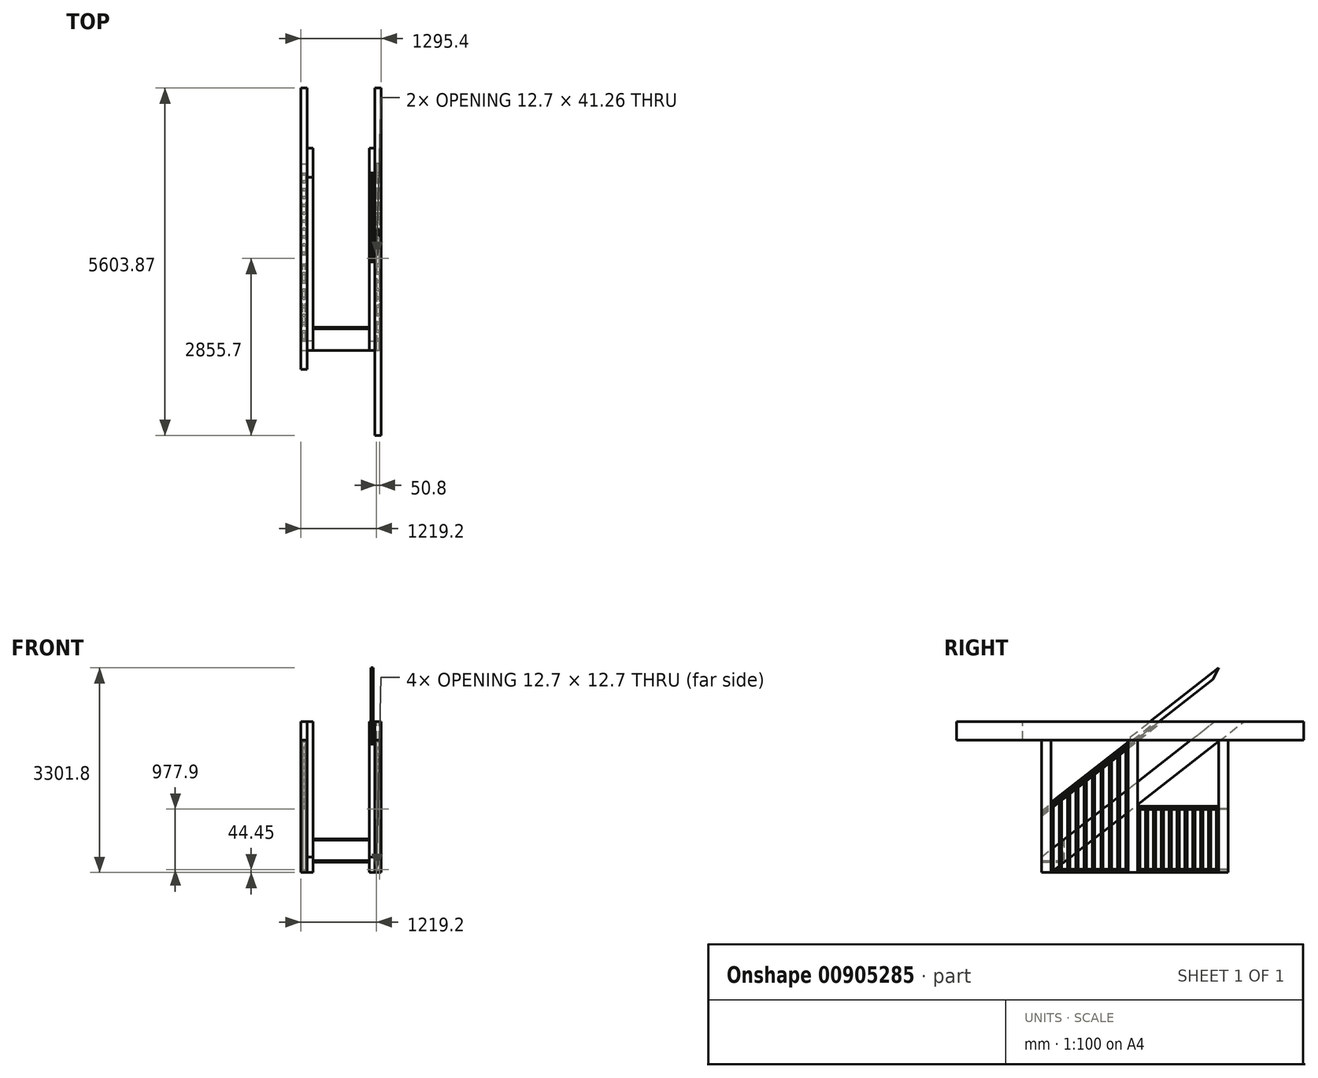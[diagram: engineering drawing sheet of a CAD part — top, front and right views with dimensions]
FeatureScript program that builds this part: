
annotation { "Feature Type Name" : "Feature", "Feature Type Description" : "" }
export const myFeature = defineFeature(function(context is Context, id is Id, definition is map)
    precondition{}
    {
        {
            var Q0;
            Q0=qCreatedBy(makeId("Front.planeOp"),FACE);
            var sketch = newSketch(context, id + "F0", { "sketchPlane" : qUnion([Q0])});
            skLineSegment(sketch, "E0", {"start": v(-546.1, 0) * mm, "end": v(546.1, 0) * mm});
            skSolve(sketch);
        }
        {
            var Q0;
            Q0=sQuery(id+"F0.wireOp",VERTEX,"E0.end");
            var Q1;
            Q1=qCreatedBy(makeId("Right.planeOp"),FACE);
            cPlane(context, id + "F1", {"entities" : qUnion([Q0, Q1]), "cplaneType" : CPlaneType.PLANE_POINT, "offset" : 25.4 * mm, "width" : 152.4 * mm, "height" : 152.4 * mm});
        }
        {
            var Q0;
            Q0=qCreatedBy(id+"F1.planeOp",FACE);
            var sketch = newSketch(context, id + "F2", { "sketchPlane" : qUnion([Q0])});
            skLineSegment(sketch, "E1.bottom", {"start": v(0, 0) * mm, "end": v(152.4, 0) * mm});
            skLineSegment(sketch, "E1.top", {"start": v(0, 2133.6) * mm, "end": v(152.4, 2133.6) * mm});
            skLineSegment(sketch, "E1.left", {"start": v(0, 0) * mm, "end": v(0, 2133.6) * mm});
            skLineSegment(sketch, "E1.right", {"start": v(152.4, 0) * mm, "end": v(152.4, 2133.6) * mm});
            skLineSegment(sketch, "E2.bottom", {"start": v(1397, 0) * mm, "end": v(1552.58, 0) * mm});
            skLineSegment(sketch, "E2.top", {"start": v(1397, 2133.6) * mm, "end": v(1552.57, 2133.6) * mm});
            skLineSegment(sketch, "E2.left", {"start": v(1397, 0) * mm, "end": v(1397, 2133.6) * mm});
            skLineSegment(sketch, "E2.right", {"start": v(1552.58, 0) * mm, "end": v(1552.57, 2133.6) * mm});
            skLineSegment(sketch, "E3.bottom", {"start": v(2860.68, 0) * mm, "end": v(3013.08, 0) * mm});
            skLineSegment(sketch, "E3.top", {"start": v(2860.68, 2133.6) * mm, "end": v(3013.07, 2133.6) * mm});
            skLineSegment(sketch, "E3.left", {"start": v(2860.68, 0) * mm, "end": v(2860.68, 2133.6) * mm});
            skLineSegment(sketch, "E3.right", {"start": v(3013.08, 0) * mm, "end": v(3013.07, 2133.6) * mm});
            skLineSegment(sketch, "E4.bottom", {"start": v(-1371.6, 2432.05) * mm, "end": v(4232.28, 2432.05) * mm});
            skLineSegment(sketch, "E4.top", {"start": v(-1371.6, 2133.6) * mm, "end": v(4232.28, 2133.6) * mm, "construction": true});
            skLineSegment(sketch, "E4.left", {"start": v(-1371.6, 2432.05) * mm, "end": v(-1371.6, 2133.6) * mm});
            skLineSegment(sketch, "E4.right", {"start": v(4232.28, 2432.05) * mm, "end": v(4232.28, 2133.6) * mm});
            skSolve(sketch);
        }
        {
            var Q0;
            Q0=qSketchRegion(id+"F2",true);
            extrude(context, id + "F3", {"entities" : qUnion([Q0]), "depth" : 101.6 * mm, "offsetDistance" : 25.4 * mm});
        }
        {
            var Q0;
            Q0=sQuery(id+"F0.wireOp",VERTEX,"E0.start");
            var Q1;
            Q1=qCreatedBy(makeId("Right.planeOp"),FACE);
            cPlane(context, id + "F4", {"entities" : qUnion([Q0, Q1]), "cplaneType" : CPlaneType.PLANE_POINT, "offset" : 25.4 * mm, "width" : 152.4 * mm, "height" : 152.4 * mm});
        }
        {
            var Q0;
            Q0=qCreatedBy(id+"F4.planeOp",FACE);
            var sketch = newSketch(context, id + "F5", { "sketchPlane" : qUnion([Q0])});
            skLineSegment(sketch, "E5.bottom", {"start": v(1390.65, 0) * mm, "end": v(1543.05, 0) * mm});
            skLineSegment(sketch, "E5.top", {"start": v(1390.65, 2133.6) * mm, "end": v(1543.05, 2133.6) * mm});
            skLineSegment(sketch, "E5.left", {"start": v(1390.65, 0) * mm, "end": v(1390.65, 2133.6) * mm});
            skLineSegment(sketch, "E5.right", {"start": v(1543.05, 0) * mm, "end": v(1543.05, 2133.6) * mm});
            skLineSegment(sketch, "E6.bottom", {"start": v(2863.85, 0) * mm, "end": v(3009.9, 0) * mm});
            skLineSegment(sketch, "E6.top", {"start": v(2863.85, 2133.6) * mm, "end": v(3009.9, 2133.6) * mm});
            skLineSegment(sketch, "E6.left", {"start": v(2863.85, 0) * mm, "end": v(2863.85, 2133.6) * mm});
            skLineSegment(sketch, "E6.right", {"start": v(3009.9, 0) * mm, "end": v(3009.9, 2133.6) * mm});
            skLineSegment(sketch, "E7.0.0", {"start": v(152.4, 2133.6) * mm, "end": v(0, 2133.6) * mm});
            skLineSegment(sketch, "E7.0.1", {"start": v(0, 2133.6) * mm, "end": v(0, 0) * mm});
            skLineSegment(sketch, "E7.0.2", {"start": v(0, 0) * mm, "end": v(152.4, 0) * mm});
            skLineSegment(sketch, "E7.0.3", {"start": v(152.4, 0) * mm, "end": v(152.4, 2133.6) * mm});
            skSolve(sketch);
        }
        {
            var Q0;
            Q0=qSketchRegion(id+"F5",true);
            extrude(context, id + "F6", {"entities" : qUnion([Q0]), "oppositeDirection" : true, "depth" : 101.6 * mm, "offsetDistance" : 25.4 * mm});
        }
        {
            var Q0;
            Q0=qCreatedBy(id+"F1.planeOp",FACE);
            var sketch = newSketch(context, id + "F7", { "sketchPlane" : qUnion([Q0])});
            skLineSegment(sketch, "E8.0", {"start": v(-1371.6, 2133.6) * mm, "end": v(4232.28, 2133.6) * mm});
            skLineSegment(sketch, "E9.0", {"start": v(-1371.6, 2432.05) * mm, "end": v(-1371.6, 2133.6) * mm});
            skLineSegment(sketch, "E10.0", {"start": v(-1371.6, 2432.05) * mm, "end": v(4232.28, 2432.05) * mm});
            skLineSegment(sketch, "E11.0", {"start": v(4232.28, 2432.05) * mm, "end": v(4232.28, 2133.6) * mm});
            skSolve(sketch);
        }
        {
            var Q0;
            Q0=makeQuery(id+"F7.imprint","IMPRINT",FACE,{"disambiguationData":[TD([[makeQuery(id+"F7.imprint","IMPRINT",EDGE,{"derivedFrom":sQuery(id+"F7.wireOp",EDGE,"E8.0")}),1.0]])]});
            var Q1;
            Q1=makeQuery(id+"F3.opExtrude","CAP_FACE",FACE,{"disambiguationData":[OSD([sQuery(id+"F2.wireOp",EDGE,"E1.bottom"),sQuery(id+"F2.wireOp",EDGE,"E1.top"),sQuery(id+"F2.wireOp",EDGE,"E1.left"),sQuery(id+"F2.wireOp",EDGE,"E1.right")])],"isStart":false});
            extrude(context, id + "F8", {"entities" : qUnion([Q0]), "endBound" : BoundingType.UP_TO_SURFACE, "depth" : 25.4 * mm, "endBoundEntityFace" : qUnion([Q1]), "offsetDistance" : 25.4 * mm});
        }
        {
            var Q0;
            Q0=qCreatedBy(id+"F4.planeOp",FACE);
            var sketch = newSketch(context, id + "F9", { "sketchPlane" : qUnion([Q0])});
            skLineSegment(sketch, "E12.0.0", {"start": v(4232.28, 2432.05) * mm, "end": v(4232.28, 2133.6) * mm});
            skLineSegment(sketch, "E12.0.1", {"start": v(4232.28, 2133.6) * mm, "end": v(-304.8, 2133.6) * mm});
            skLineSegment(sketch, "E12.0.3", {"start": v(-304.8, 2432.05) * mm, "end": v(4232.28, 2432.05) * mm});
            skLineSegment(sketch, "E13", {"start": v(-304.8, 2432.05) * mm, "end": v(-304.8, 2133.6) * mm});
            skPoint(sketch, "E12.0.2.end.orphan", {"position": v(-1371.6, 2432.05) * mm});
            skPoint(sketch, "E14.orphan", {"position": v(-1371.6, 2133.6) * mm});
            skSolve(sketch);
        }
        {
            var Q0;
            Q0=qSketchRegion(id+"F9",true);
            var Q1;
            Q1=makeQuery(id+"F6.opExtrude","CAP_FACE",FACE,{"disambiguationData":[OSD([sQuery(id+"F5.wireOp",EDGE,"E7.0.0"),sQuery(id+"F5.wireOp",EDGE,"E7.0.1"),sQuery(id+"F5.wireOp",EDGE,"E7.0.2"),sQuery(id+"F5.wireOp",EDGE,"E7.0.3")])],"isStart":false});
            extrude(context, id + "F10", {"entities" : qUnion([Q0]), "endBound" : BoundingType.UP_TO_SURFACE, "oppositeDirection" : true, "depth" : 25.4 * mm, "endBoundEntityFace" : qUnion([Q1]), "offsetDistance" : 25.4 * mm});
        }
        {
            var Q0;
            Q0=qCreatedBy(id+"F1.planeOp",FACE);
            var sketch = newSketch(context, id + "F11", { "sketchPlane" : qUnion([Q0])});
            skLineSegment(sketch, "E15.0", {"start": v(0, 0) * mm, "end": v(0, 251.61) * mm});
            skLineSegment(sketch, "E16", {"start": v(0, 251.61) * mm, "end": v(2790.83, 2432.05) * mm});
            skLineSegment(sketch, "E17", {"start": v(152.4, 0) * mm, "end": v(3265.28, 2432.05) * mm});
            skPoint(sketch, "E18.orphan", {"position": v(0, 2133.6) * mm});
            skPoint(sketch, "E19.orphan", {"position": v(152.4, 2133.6) * mm});
            skLineSegment(sketch, "E20.0", {"start": v(0, 0) * mm, "end": v(152.4, 0) * mm});
            skLineSegment(sketch, "E21.0", {"start": v(2790.83, 2432.05) * mm, "end": v(3265.28, 2432.05) * mm});
            skPoint(sketch, "E22.orphan", {"position": v(4232.28, 2432.05) * mm});
            skPoint(sketch, "E23.orphan", {"position": v(-1371.6, 2432.05) * mm});
            skPoint(sketch, "E24.0.end.orphan", {"position": v(3013.07, 2133.6) * mm});
            skPoint(sketch, "E24.0.start.orphan", {"position": v(3013.08, 0) * mm});
            skSolve(sketch);
        }
        {
            var Q0;
            Q0=qSketchRegion(id+"F11",true);
            extrude(context, id + "F12", {"entities" : qUnion([Q0]), "oppositeDirection" : true, "depth" : 92.07 * mm, "offsetDistance" : 25.4 * mm});
        }
        {
            var Q0;
            Q0=makeQuery(id+"F12.opExtrude","SWEPT_BODY",BODY,{"disambiguationData":[OSD([sQuery(id+"F11.wireOp",EDGE,"E15.0"),sQuery(id+"F11.wireOp",EDGE,"E16"),sQuery(id+"F11.wireOp",EDGE,"E17"),sQuery(id+"F11.wireOp",EDGE,"E20.0"),sQuery(id+"F11.wireOp",EDGE,"E21.0")])]});
            var Q1;
            Q1=qCreatedBy(makeId("Right.planeOp"),FACE);
            mirror(context, id + "F13", {"entities" : qUnion([Q0]), "mirrorPlane" : qUnion([Q1])});
        }
        {
            var Q0;
            Q0=makeQuery(id+"F3.opExtrude","CAP_FACE",FACE,{"disambiguationData":[OSD([sQuery(id+"F2.wireOp",EDGE,"E1.bottom"),sQuery(id+"F2.wireOp",EDGE,"E1.top"),sQuery(id+"F2.wireOp",EDGE,"E1.left"),sQuery(id+"F2.wireOp",EDGE,"E1.right")])],"isStart":false});
            var Q1;
            Q1=makeQuery(id+"F2.imprint","IMPRINT",FACE,{"disambiguationData":[TD([[makeQuery(id+"F2.imprint","IMPRINT",EDGE,{"derivedFrom":sQuery(id+"F2.wireOp",EDGE,"E1.bottom")}),1.0]])]});
            cPlane(context, id + "F14", {"entities" : qUnion([Q0, Q1]), "cplaneType" : CPlaneType.MID_PLANE, "offset" : 25.4 * mm, "width" : 152.4 * mm, "height" : 152.4 * mm});
        }
        {
            var Q0;
            Q0=qCreatedBy(id+"F14.planeOp",FACE);
            var sketch = newSketch(context, id + "F15", { "sketchPlane" : qUnion([Q0])});
            skLineSegment(sketch, "E25.0", {"start": v(152.4, 1028.7) * mm, "end": v(152.4, 1066.8) * mm, "construction": true});
            skLineSegment(sketch, "E26.0", {"start": v(1397, 1028.7) * mm, "end": v(1397, 1066.8) * mm, "construction": true});
            skLineSegment(sketch, "E27.bottom", {"start": v(152.4, 1066.8) * mm, "end": v(1397, 1066.8) * mm, "construction": true});
            skLineSegment(sketch, "E27.top", {"start": v(152.4, 1028.7) * mm, "end": v(1397, 1028.7) * mm, "construction": true});
            skPoint(sketch, "E28.orphan", {"position": v(152.4, 2133.6) * mm});
            skPoint(sketch, "E29.orphan", {"position": v(1397, 2133.6) * mm});
            skPoint(sketch, "E30.orphan", {"position": v(1397, 0) * mm});
            skPoint(sketch, "E31.orphan", {"position": v(152.4, 0) * mm});
            skLineSegment(sketch, "E32.bottom", {"start": v(1552.58, 1066.8) * mm, "end": v(2860.68, 1066.8) * mm});
            skLineSegment(sketch, "E32.top", {"start": v(1552.58, 1028.7) * mm, "end": v(2860.68, 1028.7) * mm});
            skLineSegment(sketch, "E32.left", {"start": v(1552.58, 1066.8) * mm, "end": v(1552.58, 1028.7) * mm});
            skLineSegment(sketch, "E32.right", {"start": v(2860.68, 1066.8) * mm, "end": v(2860.68, 1028.7) * mm});
            skLineSegment(sketch, "E33.bottom", {"start": v(152.4, 38.1) * mm, "end": v(1397, 38.1) * mm});
            skLineSegment(sketch, "E33.top", {"start": v(152.4, 0) * mm, "end": v(1397, 0) * mm});
            skLineSegment(sketch, "E33.left", {"start": v(152.4, 38.1) * mm, "end": v(152.4, 0) * mm});
            skLineSegment(sketch, "E33.right", {"start": v(1397, 38.1) * mm, "end": v(1397, 0) * mm});
            skLineSegment(sketch, "E34.bottom", {"start": v(1552.58, 38.1) * mm, "end": v(2860.68, 38.1) * mm});
            skLineSegment(sketch, "E34.top", {"start": v(1552.58, 0) * mm, "end": v(2860.68, 0) * mm});
            skLineSegment(sketch, "E34.left", {"start": v(1552.58, 38.1) * mm, "end": v(1552.58, 0) * mm});
            skLineSegment(sketch, "E34.right", {"start": v(2860.68, 38.1) * mm, "end": v(2860.68, 0) * mm});
            skLineSegment(sketch, "E35", {"start": v(152.4, 1028.7) * mm, "end": v(1397, 2001.09) * mm});
            skLineSegment(sketch, "E36", {"start": v(1397, 2105.85) * mm, "end": v(1397, 2001.09) * mm});
            skLineSegment(sketch, "E37", {"start": v(152.4, 1028.7) * mm, "end": v(152.4, 1066.8) * mm});
            skLineSegment(sketch, "E38", {"start": v(152.4, 1133.46) * mm, "end": v(1397, 2105.85) * mm});
            skLineSegment(sketch, "E39", {"start": v(264.57, 1221.1) * mm, "end": v(315.4, 1156.05) * mm, "construction": true});
            skLineSegment(sketch, "E40", {"start": v(152.4, 1133.46) * mm, "end": v(152.4, 1028.7) * mm});
            skLineSegment(sketch, "E41", {"start": v(152.4, 1028.7) * mm, "end": v(101.58, 1093.75) * mm, "construction": true});
            skSolve(sketch);
        }
        {
            var Q0;
            Q0=makeQuery(id+"F6.opExtrude","CAP_FACE",FACE,{"disambiguationData":[OSD([sQuery(id+"F5.wireOp",EDGE,"E7.0.0"),sQuery(id+"F5.wireOp",EDGE,"E7.0.1"),sQuery(id+"F5.wireOp",EDGE,"E7.0.2"),sQuery(id+"F5.wireOp",EDGE,"E7.0.3")])],"isStart":false});
            var Q1;
            Q1=makeQuery(id+"F6.opExtrude","CAP_FACE",FACE,{"disambiguationData":[OSD([sQuery(id+"F5.wireOp",EDGE,"E7.0.0"),sQuery(id+"F5.wireOp",EDGE,"E7.0.1"),sQuery(id+"F5.wireOp",EDGE,"E7.0.2"),sQuery(id+"F5.wireOp",EDGE,"E7.0.3")])],"isStart":true});
            cPlane(context, id + "F16", {"entities" : qUnion([Q0, Q1]), "cplaneType" : CPlaneType.MID_PLANE, "offset" : 25.4 * mm, "width" : 152.4 * mm, "height" : 152.4 * mm});
        }
        {
            var Q0;
            Q0=makeQuery(id+"F12.opExtrude","CAP_FACE",FACE,{"disambiguationData":[OSD([sQuery(id+"F11.wireOp",EDGE,"E15.0"),sQuery(id+"F11.wireOp",EDGE,"E16"),sQuery(id+"F11.wireOp",EDGE,"E17"),sQuery(id+"F11.wireOp",EDGE,"E20.0"),sQuery(id+"F11.wireOp",EDGE,"E21.0")])],"isStart":false});
            var Q1;
            Q1=makeQuery(id+"F12.opExtrude","CAP_FACE",FACE,{"disambiguationData":[OSD([sQuery(id+"F11.wireOp",EDGE,"E15.0"),sQuery(id+"F11.wireOp",EDGE,"E16"),sQuery(id+"F11.wireOp",EDGE,"E17"),sQuery(id+"F11.wireOp",EDGE,"E20.0"),sQuery(id+"F11.wireOp",EDGE,"E21.0")])],"isStart":true});
            cPlane(context, id + "F17", {"entities" : qUnion([Q0, Q1]), "cplaneType" : CPlaneType.MID_PLANE, "offset" : 25.4 * mm, "width" : 152.4 * mm, "height" : 152.4 * mm});
        }
        {
            var Q0;
            Q0=qCreatedBy(id+"F17.planeOp",FACE);
            var sketch = newSketch(context, id + "F18", { "sketchPlane" : qUnion([Q0])});
            skLineSegment(sketch, "E42.0", {"start": v(0, 364.43) * mm, "end": v(-1430.34, 1481.93) * mm, "construction": true});
            skLineSegment(sketch, "E43.0", {"start": v(0, 1066.8) * mm, "end": v(-1430.34, 2184.3) * mm, "construction": true});
            skLineSegment(sketch, "E44.0", {"start": v(0, 364.43) * mm, "end": v(0, 1066.8) * mm, "construction": true});
            skPoint(sketch, "E45.orphan", {"position": v(0, 2133.6) * mm});
            skPoint(sketch, "E46.orphan", {"position": v(0, 0) * mm});
            skLineSegment(sketch, "E47", {"start": v(-2860.68, 3301.8) * mm, "end": v(-2860.68, 2599.43) * mm});
            skLineSegment(sketch, "E48.0", {"start": v(-88.9, 1023.44) * mm, "end": v(-1430.34, 2071.49) * mm, "construction": true});
            skLineSegment(sketch, "E49.0", {"start": v(-88.9, 537.03) * mm, "end": v(-88.9, 1023.44) * mm, "construction": true});
            skLineSegment(sketch, "E50.trimOffspring", {"start": v(-2771.78, 3119.53) * mm, "end": v(-2771.78, 2633.12) * mm});
            skLineSegment(sketch, "E51.trimOffspring", {"start": v(-88.9, 537.03) * mm, "end": v(-1430.34, 1585.08) * mm, "construction": true});
            skLineSegment(sketch, "E52", {"start": v(-88.9, 1023.44) * mm, "end": v(0, 1066.8) * mm, "construction": true});
            skLineSegment(sketch, "E53", {"start": v(0, 364.43) * mm, "end": v(-88.9, 537.03) * mm, "construction": true});
            skLineSegment(sketch, "E54", {"start": v(-2771.78, 3119.53) * mm, "end": v(-2860.68, 3301.8) * mm});
            skLineSegment(sketch, "E55", {"start": v(-2771.78, 2633.12) * mm, "end": v(-2860.68, 2599.43) * mm});
            skPoint(sketch, "E56.0.start.orphan", {"position": v(-1552.58, 0) * mm});
            skPoint(sketch, "E57.0.start.orphan", {"position": v(-1397, 0) * mm});
            skLineSegment(sketch, "E58", {"start": v(-1397, 2045.44) * mm, "end": v(-1552.57, 2045.44) * mm, "construction": true});
            skLineSegment(sketch, "E59", {"start": v(-1474.79, 2045.44) * mm, "end": v(-1474.79, 1619.8) * mm, "construction": true});
            skLineSegment(sketch, "E60", {"start": v(-1430.34, 2184.3) * mm, "end": v(-1430.34, 1481.93) * mm});
            skLineSegment(sketch, "E61.MirrorCS", {"start": v(-1519.24, 2140.94) * mm, "end": v(-1519.24, 1654.53) * mm});
            skLineSegment(sketch, "E62", {"start": v(-1474.79, 1619.8) * mm, "end": v(-1238.8, 1921.85) * mm, "construction": true});
            skPoint(sketch, "E63.orphan", {"position": v(-1430.34, 2071.49) * mm});
            skPoint(sketch, "E64.orphan", {"position": v(-1430.34, 1585.08) * mm});
            skLineSegment(sketch, "E65", {"start": v(-1430.34, 2184.3) * mm, "end": v(-2860.68, 3301.8) * mm});
            skLineSegment(sketch, "E66", {"start": v(-1430.34, 2071.49) * mm, "end": v(-2771.78, 3119.53) * mm});
            skLineSegment(sketch, "E67", {"start": v(-1430.34, 1585.08) * mm, "end": v(-2771.78, 2633.12) * mm});
            skLineSegment(sketch, "E68", {"start": v(-1430.34, 1481.93) * mm, "end": v(-2860.68, 2599.43) * mm});
            skLineSegment(sketch, "E69", {"start": v(-1772.36, 1852.3) * mm, "end": v(-1552.58, 2133.6) * mm, "construction": true});
            skLineSegment(sketch, "E70.0", {"start": v(1371.6, 2133.6) * mm, "end": v(-4232.28, 2133.6) * mm, "construction": true});
            skLineSegment(sketch, "E71.0", {"start": v(-1552.58, 0) * mm, "end": v(-1552.57, 2133.6) * mm, "construction": true});
            skSolve(sketch);
        }
        {
            var Q0;
            {var subQ5=sQuery(id+"F18.wireOp",EDGE,"E54");Q0=makeQuery(id+"F18.imprint","IMPRINT",FACE,{"disambiguationData":[TD([[makeQuery(id+"F18.imprint","IMPRINT",EDGE,{"derivedFrom":subQ5}),-1.0]])]});}
            extrude(context, id + "F19", {"entities" : qUnion([Q0]), "depth" : 38.1 * mm, "offsetDistance" : 25.4 * mm, "symmetric" : true});
        }
        {
            var Q0;
            Q0=qCreatedBy(makeId("Right.planeOp"),FACE);
            var sketch = newSketch(context, id + "F20", { "sketchPlane" : qUnion([Q0])});
            skLineSegment(sketch, "E72", {"start": v(0, 170.54) * mm, "end": v(370.68, 170.54) * mm});
            skLineSegment(sketch, "E73", {"start": v(370.68, 170.54) * mm, "end": v(370.68, 541.22) * mm});
            skLineSegment(sketch, "E74.0", {"start": v(345.28, 195.94) * mm, "end": v(345.28, 521.37) * mm});
            skLineSegment(sketch, "E75.0", {"start": v(0, 195.94) * mm, "end": v(345.28, 195.94) * mm});
            skLineSegment(sketch, "E76.0", {"start": v(345.28, 521.37) * mm, "end": v(370.68, 541.22) * mm});
            skPoint(sketch, "E77.orphan", {"position": v(2790.83, 2432.05) * mm});
            skPoint(sketch, "E78.orphan", {"position": v(0, 251.61) * mm});
            skLineSegment(sketch, "E79.0", {"start": v(0, 170.54) * mm, "end": v(0, 195.94) * mm});
            skPoint(sketch, "E80.orphan", {"position": v(0, 2133.6) * mm});
            skPoint(sketch, "E81.orphan", {"position": v(0, 0) * mm});
            skSolve(sketch);
        }
        {
            var Q0;
            Q0=qSketchRegion(id+"F20",true);
            extrude(context, id + "F21", {"entities" : qUnion([Q0]), "endBound" : BoundingType.UP_TO_NEXT, "depth" : 25.4 * mm, "offsetDistance" : 25.4 * mm, "hasSecondDirection" : true, "secondDirectionBound" : BoundingType.UP_TO_NEXT, "secondDirectionOppositeDirection" : true, "secondDirectionDepth" : 25.4 * mm});
        }
        {
            var Q0;
            Q0=qSketchRegion(id+"F15",true);
            extrude(context, id + "F22", {"entities" : qUnion([Q0]), "depth" : 63.5 * mm, "offsetDistance" : 25.4 * mm, "symmetric" : true});
        }
        {
            var Q0;
            Q0=makeQuery(id+"F22.opExtrude","SWEPT_FACE",FACE,{"disambiguationData":[OSD([sQuery(id+"F15.wireOp",EDGE,"E33.left")])]});
            var sketch = newSketch(context, id + "F23", { "sketchPlane" : qUnion([Q0])});
            skLineSegment(sketch, "E82", {"start": v(596.9, 38.1) * mm, "end": v(596.9, 64.33) * mm, "construction": true});
            skArc(sketch, "E83", {"start": v(565.15, 38.1) * mm, "mid": v(568.87, 47.08) * mm, "end": v(577.85, 50.8) * mm});
            skLineSegment(sketch, "E84", {"start": v(577.85, 38.1) * mm, "end": v(577.85, 50.8) * mm});
            skLineSegment(sketch, "E85", {"start": v(565.15, 38.1) * mm, "end": v(577.85, 38.1) * mm});
            skArc(sketch, "E86.MirrorCS", {"start": v(628.65, 38.1) * mm, "mid": v(624.93, 47.08) * mm, "end": v(615.95, 50.8) * mm});
            skLineSegment(sketch, "E87.MirrorCS", {"start": v(615.95, 38.1) * mm, "end": v(615.95, 50.8) * mm});
            skLineSegment(sketch, "E88.MirrorCS", {"start": v(628.65, 38.1) * mm, "end": v(615.95, 38.1) * mm});
            skSolve(sketch);
        }
        {
            var Q0;
            Q0=sQuery(id+"F18.wireOp",EDGE,"E62");
            cPlane(context, id + "F24", {"entities" : qUnion([Q0]), "cplaneType" : CPlaneType.LINE_ANGLE, "offset" : 25.4 * mm, "angle" : 90 * degree, "width" : 152.4 * mm, "height" : 152.4 * mm});
        }
        {
            var Q0;
            Q0=qCreatedBy(id+"F24.planeOp",FACE);
            var sketch = newSketch(context, id + "F25", { "sketchPlane" : qUnion([Q0])});
            skLineSegment(sketch, "E89.bottom", {"start": v(-615.95, 716.8) * mm, "end": v(-577.85, 716.8) * mm});
            skLineSegment(sketch, "E89.top", {"start": v(-615.95, 735.85) * mm, "end": v(-577.85, 735.85) * mm});
            skLineSegment(sketch, "E89.left", {"start": v(-615.95, 716.8) * mm, "end": v(-615.95, 735.85) * mm});
            skLineSegment(sketch, "E89.right", {"start": v(-577.85, 716.8) * mm, "end": v(-577.85, 735.85) * mm});
            skLineSegment(sketch, "E90", {"start": v(-596.9, 716.8) * mm, "end": v(-596.9, 799.35) * mm, "construction": true});
            skLineSegment(sketch, "E91.0", {"start": v(-628.65, 780.3) * mm, "end": v(-628.65, 754.9) * mm});
            skLineSegment(sketch, "E92.0", {"start": v(-565.15, 780.3) * mm, "end": v(-565.15, 754.9) * mm});
            skLineSegment(sketch, "E93", {"start": v(-628.65, 780.3) * mm, "end": v(-615.95, 780.3) * mm, "construction": true});
            skLineSegment(sketch, "E94", {"start": v(-615.95, 780.3) * mm, "end": v(-615.95, 754.9) * mm, "construction": true});
            skLineSegment(sketch, "E95", {"start": v(-615.95, 754.9) * mm, "end": v(-628.65, 754.9) * mm, "construction": true});
            skLineSegment(sketch, "E96.MirrorCS", {"start": v(-565.15, 780.3) * mm, "end": v(-577.85, 780.3) * mm, "construction": true});
            skLineSegment(sketch, "E97.MirrorCS", {"start": v(-577.85, 780.3) * mm, "end": v(-577.85, 754.9) * mm, "construction": true});
            skLineSegment(sketch, "E98.MirrorCS", {"start": v(-577.85, 754.9) * mm, "end": v(-565.15, 754.9) * mm, "construction": true});
            skPoint(sketch, "E99.orphan", {"position": v(-565.15, 799.35) * mm});
            skPoint(sketch, "E100.orphan", {"position": v(-565.15, 716.8) * mm});
            skPoint(sketch, "E101.orphan", {"position": v(-628.65, 716.8) * mm});
            skPoint(sketch, "E102.orphan", {"position": v(-628.65, 799.35) * mm});
            skArc(sketch, "E103", {"start": v(-628.65, 754.9) * mm, "mid": v(-615.95, 767.6) * mm, "end": v(-628.65, 780.3) * mm});
            skArc(sketch, "E104", {"start": v(-565.15, 780.3) * mm, "mid": v(-577.85, 767.6) * mm, "end": v(-565.15, 754.9) * mm});
            skSolve(sketch);
        }
        {
            var Q0;
            Q0 = qSketchRegion(id + "F25", true);
            extrude(context, id + "F26", {"entities" : qUnion([Q0]), "operationType" : NewBodyOperationType.REMOVE, "endBound" : BoundingType.THROUGH_ALL, "oppositeDirection" : true, "depth" : 25.4 * mm, "offsetDistance" : 25.4 * mm, "hasSecondDirection" : true, "secondDirectionBound" : BoundingType.THROUGH_ALL, "secondDirectionOppositeDirection" : false, "secondDirectionDepth" : 25.4 * mm});
        }
        {
            var Q0;
            Q0=makeQuery(id+"F22.opExtrude","SWEPT_FACE",FACE,{"disambiguationData":[OSD([sQuery(id+"F15.wireOp",EDGE,"E33.bottom")])]});
            var sketch = newSketch(context, id + "F27", { "sketchPlane" : qUnion([Q0])});
            skLineSegment(sketch, "E105", {"start": v(596.9, 152.4) * mm, "end": v(596.9, 171.45) * mm, "construction": true});
            skLineSegment(sketch, "E106.bottom", {"start": v(577.85, 190.5) * mm, "end": v(615.95, 190.5) * mm});
            skLineSegment(sketch, "E106.top", {"start": v(577.85, 152.4) * mm, "end": v(615.95, 152.4) * mm});
            skLineSegment(sketch, "E106.left", {"start": v(577.85, 190.5) * mm, "end": v(577.85, 152.4) * mm});
            skLineSegment(sketch, "E106.right", {"start": v(615.95, 190.5) * mm, "end": v(615.95, 152.4) * mm});
            skPoint(sketch, "E106.middle", {"position": v(596.9, 171.45) * mm});
            skLineSegment(sketch, "E107.direction1", {"start": v(577.85, 152.4) * mm, "end": v(596.9, 152.4) * mm, "construction": true});
            skLineSegment(sketch, "E108", {"start": v(596.9, 1397) * mm, "end": v(596.9, 1377.95) * mm, "construction": true});
            skLineSegment(sketch, "E109.bottom", {"start": v(615.95, 1358.9) * mm, "end": v(577.85, 1358.9) * mm});
            skLineSegment(sketch, "E109.top", {"start": v(615.95, 1397) * mm, "end": v(577.85, 1397) * mm});
            skLineSegment(sketch, "E109.left", {"start": v(615.95, 1358.9) * mm, "end": v(615.95, 1397) * mm});
            skLineSegment(sketch, "E109.right", {"start": v(577.85, 1358.9) * mm, "end": v(577.85, 1397) * mm});
            skPoint(sketch, "E109.middle", {"position": v(596.9, 1377.95) * mm});
            skLineSegment(sketch, "E110", {"start": v(596.9, 171.45) * mm, "end": v(596.9, 305.51) * mm, "construction": true});
            skLineSegment(sketch, "E111", {"start": v(596.9, 1377.95) * mm, "end": v(596.9, 1243.89) * mm, "construction": true});
            skLineSegment(sketch, "E112.bottom", {"start": v(577.85, 324.56) * mm, "end": v(615.95, 324.56) * mm});
            skLineSegment(sketch, "E112.top", {"start": v(577.85, 286.46) * mm, "end": v(615.95, 286.46) * mm});
            skLineSegment(sketch, "E112.left", {"start": v(577.85, 324.56) * mm, "end": v(577.85, 286.46) * mm});
            skLineSegment(sketch, "E112.right", {"start": v(615.95, 324.56) * mm, "end": v(615.95, 286.46) * mm});
            skPoint(sketch, "E112.middle", {"position": v(596.9, 305.51) * mm});
            skLineSegment(sketch, "E113.0.1.0", {"start": v(577.85, 458.62) * mm, "end": v(615.95, 458.62) * mm});
            skLineSegment(sketch, "E113.0.1.1", {"start": v(577.85, 458.62) * mm, "end": v(577.85, 420.52) * mm});
            skLineSegment(sketch, "E113.0.1.2", {"start": v(577.85, 420.52) * mm, "end": v(615.95, 420.52) * mm});
            skLineSegment(sketch, "E113.0.1.3", {"start": v(615.95, 458.62) * mm, "end": v(615.95, 420.52) * mm});
            skPoint(sketch, "E113.0.1.4", {"position": v(596.9, 439.57) * mm});
            skLineSegment(sketch, "E113.0.2.0", {"start": v(577.85, 592.68) * mm, "end": v(615.95, 592.68) * mm});
            skLineSegment(sketch, "E113.0.2.1", {"start": v(577.85, 592.68) * mm, "end": v(577.85, 554.58) * mm});
            skLineSegment(sketch, "E113.0.2.2", {"start": v(577.85, 554.58) * mm, "end": v(615.95, 554.58) * mm});
            skLineSegment(sketch, "E113.0.2.3", {"start": v(615.95, 592.68) * mm, "end": v(615.95, 554.58) * mm});
            skPoint(sketch, "E113.0.2.4", {"position": v(596.9, 573.63) * mm});
            skLineSegment(sketch, "E113.0.3.0", {"start": v(577.85, 726.74) * mm, "end": v(615.95, 726.74) * mm});
            skLineSegment(sketch, "E113.0.3.1", {"start": v(577.85, 726.74) * mm, "end": v(577.85, 688.64) * mm});
            skLineSegment(sketch, "E113.0.3.2", {"start": v(577.85, 688.64) * mm, "end": v(615.95, 688.64) * mm});
            skLineSegment(sketch, "E113.0.3.3", {"start": v(615.95, 726.74) * mm, "end": v(615.95, 688.64) * mm});
            skPoint(sketch, "E113.0.3.4", {"position": v(596.9, 707.7) * mm});
            skLineSegment(sketch, "E113.0.4.0", {"start": v(577.85, 860.8) * mm, "end": v(615.95, 860.8) * mm});
            skLineSegment(sketch, "E113.0.4.1", {"start": v(577.85, 860.8) * mm, "end": v(577.85, 822.7) * mm});
            skLineSegment(sketch, "E113.0.4.2", {"start": v(577.85, 822.7) * mm, "end": v(615.95, 822.7) * mm});
            skLineSegment(sketch, "E113.0.4.3", {"start": v(615.95, 860.8) * mm, "end": v(615.95, 822.7) * mm});
            skPoint(sketch, "E113.0.4.4", {"position": v(596.9, 841.76) * mm});
            skLineSegment(sketch, "E113.0.5.0", {"start": v(577.85, 994.87) * mm, "end": v(615.95, 994.87) * mm});
            skLineSegment(sketch, "E113.0.5.1", {"start": v(577.85, 994.87) * mm, "end": v(577.85, 956.77) * mm});
            skLineSegment(sketch, "E113.0.5.2", {"start": v(577.85, 956.77) * mm, "end": v(615.95, 956.77) * mm});
            skLineSegment(sketch, "E113.0.5.3", {"start": v(615.95, 994.87) * mm, "end": v(615.95, 956.77) * mm});
            skPoint(sketch, "E113.0.5.4", {"position": v(596.9, 975.82) * mm});
            skLineSegment(sketch, "E113.0.6.0", {"start": v(577.85, 1128.93) * mm, "end": v(615.95, 1128.93) * mm});
            skLineSegment(sketch, "E113.0.6.1", {"start": v(577.85, 1128.93) * mm, "end": v(577.85, 1090.83) * mm});
            skLineSegment(sketch, "E113.0.6.2", {"start": v(577.85, 1090.83) * mm, "end": v(615.95, 1090.83) * mm});
            skLineSegment(sketch, "E113.0.6.3", {"start": v(615.95, 1128.93) * mm, "end": v(615.95, 1090.83) * mm});
            skPoint(sketch, "E113.0.6.4", {"position": v(596.9, 1109.88) * mm});
            skLineSegment(sketch, "E113.direction1", {"start": v(577.85, 286.46) * mm, "end": v(596.9, 286.46) * mm, "construction": true});
            skLineSegment(sketch, "E113.direction2", {"start": v(577.85, 286.46) * mm, "end": v(577.85, 420.52) * mm, "construction": true});
            skLineSegment(sketch, "E114.0.0.7", {"start": v(577.85, 1262.99) * mm, "end": v(615.95, 1262.99) * mm});
            skLineSegment(sketch, "E114.3.0.7", {"start": v(577.85, 1262.99) * mm, "end": v(577.85, 1224.89) * mm});
            skLineSegment(sketch, "E114.6.0.7", {"start": v(577.85, 1224.89) * mm, "end": v(615.95, 1224.89) * mm});
            skLineSegment(sketch, "E114.9.0.7", {"start": v(615.95, 1262.99) * mm, "end": v(615.95, 1224.89) * mm});
            skPoint(sketch, "E114.12.0.7", {"position": v(596.9, 1243.94) * mm});
            skSolve(sketch);
        }
        {
            var Q0;
            Q0=makeQuery(id+"F22.opExtrude","SWEPT_FACE",FACE,{"disambiguationData":[OSD([sQuery(id+"F15.wireOp",EDGE,"E34.bottom")])]});
            var sketch = newSketch(context, id + "F28", { "sketchPlane" : qUnion([Q0])});
            skLineSegment(sketch, "E115", {"start": v(596.9, 1571.62) * mm, "end": v(596.9, 1552.58) * mm, "construction": true});
            skLineSegment(sketch, "E116.bottom", {"start": v(615.95, 1590.68) * mm, "end": v(577.85, 1590.68) * mm});
            skLineSegment(sketch, "E116.top", {"start": v(615.95, 1552.58) * mm, "end": v(577.85, 1552.58) * mm});
            skLineSegment(sketch, "E116.left", {"start": v(577.85, 1552.58) * mm, "end": v(577.85, 1590.68) * mm});
            skLineSegment(sketch, "E116.right", {"start": v(615.95, 1552.58) * mm, "end": v(615.95, 1590.68) * mm});
            skPoint(sketch, "E116.middle", {"position": v(596.9, 1571.62) * mm});
            skLineSegment(sketch, "E117", {"start": v(596.9, 2860.68) * mm, "end": v(596.9, 2841.63) * mm, "construction": true});
            skLineSegment(sketch, "E118.bottom", {"start": v(577.85, 2860.68) * mm, "end": v(615.95, 2860.68) * mm});
            skLineSegment(sketch, "E118.top", {"start": v(577.85, 2822.58) * mm, "end": v(615.95, 2822.58) * mm});
            skLineSegment(sketch, "E118.left", {"start": v(577.85, 2860.68) * mm, "end": v(577.85, 2822.58) * mm});
            skLineSegment(sketch, "E118.right", {"start": v(615.95, 2860.68) * mm, "end": v(615.95, 2822.58) * mm});
            skPoint(sketch, "E118.middle", {"position": v(596.9, 2841.63) * mm});
            skLineSegment(sketch, "E119", {"start": v(596.9, 1571.62) * mm, "end": v(596.9, 1698.63) * mm, "construction": true});
            skLineSegment(sketch, "E120.bottom", {"start": v(577.85, 1717.68) * mm, "end": v(615.95, 1717.68) * mm});
            skLineSegment(sketch, "E120.top", {"start": v(577.85, 1679.58) * mm, "end": v(615.95, 1679.58) * mm});
            skLineSegment(sketch, "E120.left", {"start": v(577.85, 1717.68) * mm, "end": v(577.85, 1679.58) * mm});
            skLineSegment(sketch, "E120.right", {"start": v(615.95, 1717.68) * mm, "end": v(615.95, 1679.58) * mm});
            skPoint(sketch, "E120.middle", {"position": v(596.9, 1698.63) * mm});
            skLineSegment(sketch, "E121.0.1.0", {"start": v(577.85, 1844.67) * mm, "end": v(577.85, 1806.58) * mm});
            skLineSegment(sketch, "E121.0.1.1", {"start": v(577.85, 1844.67) * mm, "end": v(615.95, 1844.67) * mm});
            skLineSegment(sketch, "E121.0.1.2", {"start": v(615.95, 1844.67) * mm, "end": v(615.95, 1806.58) * mm});
            skLineSegment(sketch, "E121.0.1.3", {"start": v(577.85, 1806.58) * mm, "end": v(615.95, 1806.58) * mm});
            skLineSegment(sketch, "E121.0.2.0", {"start": v(577.85, 1971.67) * mm, "end": v(577.85, 1933.58) * mm});
            skLineSegment(sketch, "E121.0.2.1", {"start": v(577.85, 1971.67) * mm, "end": v(615.95, 1971.67) * mm});
            skLineSegment(sketch, "E121.0.2.2", {"start": v(615.95, 1971.67) * mm, "end": v(615.95, 1933.58) * mm});
            skLineSegment(sketch, "E121.0.2.3", {"start": v(577.85, 1933.58) * mm, "end": v(615.95, 1933.58) * mm});
            skLineSegment(sketch, "E121.0.3.0", {"start": v(577.85, 2098.68) * mm, "end": v(577.85, 2060.57) * mm});
            skLineSegment(sketch, "E121.0.3.1", {"start": v(577.85, 2098.68) * mm, "end": v(615.95, 2098.68) * mm});
            skLineSegment(sketch, "E121.0.3.2", {"start": v(615.95, 2098.68) * mm, "end": v(615.95, 2060.57) * mm});
            skLineSegment(sketch, "E121.0.3.3", {"start": v(577.85, 2060.57) * mm, "end": v(615.95, 2060.57) * mm});
            skLineSegment(sketch, "E121.0.4.0", {"start": v(577.85, 2225.67) * mm, "end": v(577.85, 2187.57) * mm});
            skLineSegment(sketch, "E121.0.4.1", {"start": v(577.85, 2225.67) * mm, "end": v(615.95, 2225.67) * mm});
            skLineSegment(sketch, "E121.0.4.2", {"start": v(615.95, 2225.67) * mm, "end": v(615.95, 2187.57) * mm});
            skLineSegment(sketch, "E121.0.4.3", {"start": v(577.85, 2187.57) * mm, "end": v(615.95, 2187.57) * mm});
            skLineSegment(sketch, "E121.0.5.0", {"start": v(577.85, 2352.68) * mm, "end": v(577.85, 2314.58) * mm});
            skLineSegment(sketch, "E121.0.5.1", {"start": v(577.85, 2352.68) * mm, "end": v(615.95, 2352.68) * mm});
            skLineSegment(sketch, "E121.0.5.2", {"start": v(615.95, 2352.68) * mm, "end": v(615.95, 2314.58) * mm});
            skLineSegment(sketch, "E121.0.5.3", {"start": v(577.85, 2314.58) * mm, "end": v(615.95, 2314.58) * mm});
            skLineSegment(sketch, "E121.0.6.0", {"start": v(577.85, 2479.68) * mm, "end": v(577.85, 2441.58) * mm});
            skLineSegment(sketch, "E121.0.6.1", {"start": v(577.85, 2479.68) * mm, "end": v(615.95, 2479.68) * mm});
            skLineSegment(sketch, "E121.0.6.2", {"start": v(615.95, 2479.68) * mm, "end": v(615.95, 2441.58) * mm});
            skLineSegment(sketch, "E121.0.6.3", {"start": v(577.85, 2441.58) * mm, "end": v(615.95, 2441.58) * mm});
            skLineSegment(sketch, "E121.direction1", {"start": v(577.85, 1679.58) * mm, "end": v(603.25, 1679.58) * mm, "construction": true});
            skLineSegment(sketch, "E121.direction2", {"start": v(577.85, 1679.58) * mm, "end": v(577.85, 1806.58) * mm, "construction": true});
            skLineSegment(sketch, "E122.0.0.7", {"start": v(577.85, 2606.68) * mm, "end": v(577.85, 2568.58) * mm});
            skLineSegment(sketch, "E122.3.0.7", {"start": v(577.85, 2606.68) * mm, "end": v(615.95, 2606.68) * mm});
            skLineSegment(sketch, "E122.6.0.7", {"start": v(615.95, 2606.68) * mm, "end": v(615.95, 2568.58) * mm});
            skLineSegment(sketch, "E122.9.0.7", {"start": v(577.85, 2568.58) * mm, "end": v(615.95, 2568.58) * mm});
            skLineSegment(sketch, "E123", {"start": v(577.85, 2587.62) * mm, "end": v(615.95, 2587.62) * mm, "construction": true});
            skLineSegment(sketch, "E124.0.0.8", {"start": v(577.85, 2733.67) * mm, "end": v(577.85, 2695.57) * mm});
            skLineSegment(sketch, "E124.3.0.8", {"start": v(577.85, 2733.67) * mm, "end": v(615.95, 2733.67) * mm});
            skLineSegment(sketch, "E124.6.0.8", {"start": v(615.95, 2733.67) * mm, "end": v(615.95, 2695.57) * mm});
            skLineSegment(sketch, "E124.9.0.8", {"start": v(577.85, 2695.57) * mm, "end": v(615.95, 2695.57) * mm});
            skLineSegment(sketch, "E124.0.0.9", {"start": v(577.85, 2860.67) * mm, "end": v(577.85, 2822.57) * mm});
            skLineSegment(sketch, "E124.3.0.9", {"start": v(577.85, 2860.67) * mm, "end": v(615.95, 2860.67) * mm});
            skLineSegment(sketch, "E124.6.0.9", {"start": v(615.95, 2860.67) * mm, "end": v(615.95, 2822.57) * mm});
            skLineSegment(sketch, "E124.9.0.9", {"start": v(577.85, 2822.57) * mm, "end": v(615.95, 2822.57) * mm});
            skSolve(sketch);
        }
        {
            var Q0;
            Q0=makeQuery(id+"F22.opExtrude","SWEPT_FACE",FACE,{"disambiguationData":[OSD([sQuery(id+"F15.wireOp",EDGE,"E32.left")])]});
            var sketch = newSketch(context, id + "F29", { "sketchPlane" : qUnion([Q0])});
            skLineSegment(sketch, "E125", {"start": v(596.9, 1028.7) * mm, "end": v(596.9, 1003.92) * mm, "construction": true});
            skArc(sketch, "E126", {"start": v(565.15, 1028.7) * mm, "mid": v(568.87, 1019.72) * mm, "end": v(577.85, 1016) * mm});
            skLineSegment(sketch, "E127", {"start": v(577.85, 1016) * mm, "end": v(577.85, 1028.7) * mm});
            skLineSegment(sketch, "E128", {"start": v(565.15, 1028.7) * mm, "end": v(577.85, 1028.7) * mm});
            skLineSegment(sketch, "E129.MirrorCS", {"start": v(628.65, 1028.7) * mm, "end": v(615.95, 1028.7) * mm});
            skArc(sketch, "E130.MirrorCS", {"start": v(628.65, 1028.7) * mm, "mid": v(624.93, 1019.72) * mm, "end": v(615.95, 1016) * mm});
            skLineSegment(sketch, "E131.MirrorCS", {"start": v(615.95, 1016) * mm, "end": v(615.95, 1028.7) * mm});
            skArc(sketch, "E132.0", {"start": v(628.65, 38.1) * mm, "mid": v(624.93, 47.08) * mm, "end": v(615.95, 50.8) * mm});
            skLineSegment(sketch, "E133.0", {"start": v(615.95, 38.1) * mm, "end": v(615.95, 50.8) * mm});
            skLineSegment(sketch, "E134.0", {"start": v(628.65, 38.1) * mm, "end": v(615.95, 38.1) * mm});
            skLineSegment(sketch, "E135.0", {"start": v(577.85, 38.1) * mm, "end": v(577.85, 50.8) * mm});
            skLineSegment(sketch, "E136.0", {"start": v(565.15, 38.1) * mm, "end": v(577.85, 38.1) * mm});
            skArc(sketch, "E137.0", {"start": v(565.15, 38.1) * mm, "mid": v(568.87, 47.08) * mm, "end": v(577.85, 50.8) * mm});
            skSolve(sketch);
        }
        {
            var Q0;
            Q0=qSketchRegion(id+"F27",true);
            var Q1;
            Q1=makeQuery(id+"F26.boolean.opBoolean","COPY",FACE,{"derivedFrom":makeQuery(id+"F26.opExtrude","SWEPT_FACE",FACE,{"disambiguationData":[OSD([sQuery(id+"F25.wireOp",EDGE,"E89.top")])]})});
            extrude(context, id + "F30", {"entities" : qUnion([Q0]), "endBound" : BoundingType.UP_TO_SURFACE, "depth" : 25.4 * mm, "endBoundEntityFace" : qUnion([Q1]), "offsetDistance" : 25.4 * mm});
        }
        {
            var Q0;
            Q0 = qSketchRegion(id + "F29", true);
            extrude(context, id + "F31", {"entities" : qUnion([Q0]), "operationType" : NewBodyOperationType.REMOVE, "endBound" : BoundingType.THROUGH_ALL, "oppositeDirection" : true, "depth" : 25.4 * mm, "offsetDistance" : 25.4 * mm});
        }
        {
            var Q0;
            Q0=qSketchRegion(id+"F28",true);
            var Q1;
            Q1=makeQuery(id+"F22.opExtrude","SWEPT_FACE",FACE,{"disambiguationData":[OSD([sQuery(id+"F15.wireOp",EDGE,"E32.top")])]});
            extrude(context, id + "F32", {"entities" : qUnion([Q0]), "endBound" : BoundingType.UP_TO_NEXT, "depth" : 25.4 * mm, "endBoundEntityFace" : qUnion([Q1]), "offsetDistance" : 25.4 * mm});
        }
        {
            var Q0;
            Q0=sQuery(id+"F18.wireOp",EDGE,"E69");
            cPlane(context, id + "F33", {"entities" : qUnion([Q0]), "cplaneType" : CPlaneType.LINE_ANGLE, "offset" : 25.4 * mm, "angle" : 90 * degree, "width" : 152.4 * mm, "height" : 152.4 * mm});
        }
        {
            var Q0;
            Q0=makeQuery(id+"F22.opExtrude","SWEPT_BODY",BODY,{"disambiguationData":[OSD([sQuery(id+"F15.wireOp",EDGE,"E32.bottom"),sQuery(id+"F15.wireOp",EDGE,"E32.top"),sQuery(id+"F15.wireOp",EDGE,"E32.left"),sQuery(id+"F15.wireOp",EDGE,"E32.right")])]});
            var Q1;
            Q1=makeQuery(id+"F22.opExtrude","SWEPT_BODY",BODY,{"disambiguationData":[OSD([sQuery(id+"F15.wireOp",EDGE,"E34.bottom"),sQuery(id+"F15.wireOp",EDGE,"E34.top"),sQuery(id+"F15.wireOp",EDGE,"E34.left"),sQuery(id+"F15.wireOp",EDGE,"E34.right")])]});
            var Q2;
            Q2=makeQuery(id+"F22.opExtrude","SWEPT_BODY",BODY,{"disambiguationData":[OSD([sQuery(id+"F15.wireOp",EDGE,"E33.bottom"),sQuery(id+"F15.wireOp",EDGE,"E33.top"),sQuery(id+"F15.wireOp",EDGE,"E33.left"),sQuery(id+"F15.wireOp",EDGE,"E33.right")])]});
            var Q3;
            Q3=makeQuery(id+"F22.opExtrude","SWEPT_BODY",BODY,{"disambiguationData":[OSD([sQuery(id+"F15.wireOp",EDGE,"E35"),sQuery(id+"F15.wireOp",EDGE,"E36"),sQuery(id+"F15.wireOp",EDGE,"E38"),sQuery(id+"F15.wireOp",EDGE,"E40")])]});
            var Q4;
            Q4=makeQuery(id+"F30.opExtrude","SWEPT_BODY",BODY,{"disambiguationData":[OSD([sQuery(id+"F27.wireOp",EDGE,"E106.bottom"),sQuery(id+"F27.wireOp",EDGE,"E106.top"),sQuery(id+"F27.wireOp",EDGE,"E106.left"),sQuery(id+"F27.wireOp",EDGE,"E106.right")])]});
            var Q5;
            Q5=makeQuery(id+"F30.opExtrude","SWEPT_BODY",BODY,{"disambiguationData":[OSD([sQuery(id+"F27.wireOp",EDGE,"E112.bottom"),sQuery(id+"F27.wireOp",EDGE,"E112.top"),sQuery(id+"F27.wireOp",EDGE,"E112.left"),sQuery(id+"F27.wireOp",EDGE,"E112.right")])]});
            var Q6;
            Q6=makeQuery(id+"F30.opExtrude","SWEPT_BODY",BODY,{"disambiguationData":[OSD([sQuery(id+"F27.wireOp",EDGE,"E113.0.1.0"),sQuery(id+"F27.wireOp",EDGE,"E113.0.1.1"),sQuery(id+"F27.wireOp",EDGE,"E113.0.1.2"),sQuery(id+"F27.wireOp",EDGE,"E113.0.1.3")])]});
            var Q7;
            Q7=makeQuery(id+"F30.opExtrude","SWEPT_BODY",BODY,{"disambiguationData":[OSD([sQuery(id+"F27.wireOp",EDGE,"E113.0.2.0"),sQuery(id+"F27.wireOp",EDGE,"E113.0.2.1"),sQuery(id+"F27.wireOp",EDGE,"E113.0.2.2"),sQuery(id+"F27.wireOp",EDGE,"E113.0.2.3")])]});
            var Q8;
            Q8=makeQuery(id+"F30.opExtrude","SWEPT_BODY",BODY,{"disambiguationData":[OSD([sQuery(id+"F27.wireOp",EDGE,"E113.0.3.0"),sQuery(id+"F27.wireOp",EDGE,"E113.0.3.1"),sQuery(id+"F27.wireOp",EDGE,"E113.0.3.2"),sQuery(id+"F27.wireOp",EDGE,"E113.0.3.3")])]});
            var Q9;
            Q9=makeQuery(id+"F30.opExtrude","SWEPT_BODY",BODY,{"disambiguationData":[OSD([sQuery(id+"F27.wireOp",EDGE,"E113.0.4.0"),sQuery(id+"F27.wireOp",EDGE,"E113.0.4.1"),sQuery(id+"F27.wireOp",EDGE,"E113.0.4.2"),sQuery(id+"F27.wireOp",EDGE,"E113.0.4.3")])]});
            var Q10;
            Q10=makeQuery(id+"F30.opExtrude","SWEPT_BODY",BODY,{"disambiguationData":[OSD([sQuery(id+"F27.wireOp",EDGE,"E113.0.5.0"),sQuery(id+"F27.wireOp",EDGE,"E113.0.5.1"),sQuery(id+"F27.wireOp",EDGE,"E113.0.5.2"),sQuery(id+"F27.wireOp",EDGE,"E113.0.5.3")])]});
            var Q11;
            Q11=makeQuery(id+"F30.opExtrude","SWEPT_BODY",BODY,{"disambiguationData":[OSD([sQuery(id+"F27.wireOp",EDGE,"E113.0.6.0"),sQuery(id+"F27.wireOp",EDGE,"E113.0.6.1"),sQuery(id+"F27.wireOp",EDGE,"E113.0.6.2"),sQuery(id+"F27.wireOp",EDGE,"E113.0.6.3")])]});
            var Q12;
            Q12=makeQuery(id+"F30.opExtrude","SWEPT_BODY",BODY,{"disambiguationData":[OSD([sQuery(id+"F27.wireOp",EDGE,"E114.0.0.7"),sQuery(id+"F27.wireOp",EDGE,"E114.3.0.7"),sQuery(id+"F27.wireOp",EDGE,"E114.6.0.7"),sQuery(id+"F27.wireOp",EDGE,"E114.9.0.7")])]});
            var Q13;
            Q13=makeQuery(id+"F30.opExtrude","SWEPT_BODY",BODY,{"disambiguationData":[OSD([sQuery(id+"F27.wireOp",EDGE,"E109.bottom"),sQuery(id+"F27.wireOp",EDGE,"E109.top"),sQuery(id+"F27.wireOp",EDGE,"E109.left"),sQuery(id+"F27.wireOp",EDGE,"E109.right")])]});
            var Q14;
            Q14=makeQuery(id+"F32.opExtrude","SWEPT_BODY",BODY,{"disambiguationData":[OSD([sQuery(id+"F28.wireOp",EDGE,"E116.bottom"),sQuery(id+"F28.wireOp",EDGE,"E116.top"),sQuery(id+"F28.wireOp",EDGE,"E116.left"),sQuery(id+"F28.wireOp",EDGE,"E116.right")])]});
            var Q15;
            Q15=makeQuery(id+"F32.opExtrude","SWEPT_BODY",BODY,{"disambiguationData":[OSD([sQuery(id+"F28.wireOp",EDGE,"E120.bottom"),sQuery(id+"F28.wireOp",EDGE,"E120.top"),sQuery(id+"F28.wireOp",EDGE,"E120.left"),sQuery(id+"F28.wireOp",EDGE,"E120.right")])]});
            var Q16;
            Q16=makeQuery(id+"F32.opExtrude","SWEPT_BODY",BODY,{"disambiguationData":[OSD([sQuery(id+"F28.wireOp",EDGE,"E121.0.1.0"),sQuery(id+"F28.wireOp",EDGE,"E121.0.1.1"),sQuery(id+"F28.wireOp",EDGE,"E121.0.1.2"),sQuery(id+"F28.wireOp",EDGE,"E121.0.1.3")])]});
            var Q17;
            Q17=makeQuery(id+"F32.opExtrude","SWEPT_BODY",BODY,{"disambiguationData":[OSD([sQuery(id+"F28.wireOp",EDGE,"E121.0.2.0"),sQuery(id+"F28.wireOp",EDGE,"E121.0.2.1"),sQuery(id+"F28.wireOp",EDGE,"E121.0.2.2"),sQuery(id+"F28.wireOp",EDGE,"E121.0.2.3")])]});
            var Q18;
            Q18=makeQuery(id+"F32.opExtrude","SWEPT_BODY",BODY,{"disambiguationData":[OSD([sQuery(id+"F28.wireOp",EDGE,"E121.0.3.0"),sQuery(id+"F28.wireOp",EDGE,"E121.0.3.1"),sQuery(id+"F28.wireOp",EDGE,"E121.0.3.2"),sQuery(id+"F28.wireOp",EDGE,"E121.0.3.3")])]});
            var Q19;
            Q19=makeQuery(id+"F32.opExtrude","SWEPT_BODY",BODY,{"disambiguationData":[OSD([sQuery(id+"F28.wireOp",EDGE,"E121.0.4.0"),sQuery(id+"F28.wireOp",EDGE,"E121.0.4.1"),sQuery(id+"F28.wireOp",EDGE,"E121.0.4.2"),sQuery(id+"F28.wireOp",EDGE,"E121.0.4.3")])]});
            var Q20;
            Q20=makeQuery(id+"F32.opExtrude","SWEPT_BODY",BODY,{"disambiguationData":[OSD([sQuery(id+"F28.wireOp",EDGE,"E121.0.5.0"),sQuery(id+"F28.wireOp",EDGE,"E121.0.5.1"),sQuery(id+"F28.wireOp",EDGE,"E121.0.5.2"),sQuery(id+"F28.wireOp",EDGE,"E121.0.5.3")])]});
            var Q21;
            Q21=makeQuery(id+"F32.opExtrude","SWEPT_BODY",BODY,{"disambiguationData":[OSD([sQuery(id+"F28.wireOp",EDGE,"E121.0.6.0"),sQuery(id+"F28.wireOp",EDGE,"E121.0.6.1"),sQuery(id+"F28.wireOp",EDGE,"E121.0.6.2"),sQuery(id+"F28.wireOp",EDGE,"E121.0.6.3")])]});
            var Q22;
            Q22=makeQuery(id+"F32.opExtrude","SWEPT_BODY",BODY,{"disambiguationData":[OSD([sQuery(id+"F28.wireOp",EDGE,"E122.0.0.7"),sQuery(id+"F28.wireOp",EDGE,"E122.3.0.7"),sQuery(id+"F28.wireOp",EDGE,"E122.6.0.7"),sQuery(id+"F28.wireOp",EDGE,"E122.9.0.7")])]});
            var Q23;
            Q23=makeQuery(id+"F32.opExtrude","SWEPT_BODY",BODY,{"disambiguationData":[OSD([sQuery(id+"F28.wireOp",EDGE,"E124.0.0.8"),sQuery(id+"F28.wireOp",EDGE,"E124.3.0.8"),sQuery(id+"F28.wireOp",EDGE,"E124.6.0.8"),sQuery(id+"F28.wireOp",EDGE,"E124.9.0.8")])]});
            var Q24;
            Q24=makeQuery(id+"F32.opExtrude","SWEPT_BODY",BODY,{"disambiguationData":[OSD([sQuery(id+"F28.wireOp",EDGE,"E124.0.0.9"),sQuery(id+"F28.wireOp",EDGE,"E124.3.0.9"),sQuery(id+"F28.wireOp",EDGE,"E124.6.0.9"),sQuery(id+"F28.wireOp",EDGE,"E124.9.0.9")])]});
            var Q25;
            Q25=qCreatedBy(makeId("Right.planeOp"),FACE);
            mirror(context, id + "F34", {"entities" : qUnion([Q0, Q1, Q2, Q3, Q4, Q5, Q6, Q7, Q8, Q9, Q10, Q11, Q12, Q13, Q14, Q15, Q16, Q17, Q18, Q19, Q20, Q21, Q22, Q23, Q24]), "mirrorPlane" : qUnion([Q25])});
        }
        {
            var Q0;
            Q0 = qSketchRegion(id + "F23", true);
            var Q1;
            Q1=makeQuery(id+"F22.opExtrude","SWEPT_FACE",FACE,{"disambiguationData":[OSD([sQuery(id+"F15.wireOp",EDGE,"E33.right")])]});
            extrude(context, id + "F35", {"entities" : qUnion([Q0]), "endBound" : BoundingType.UP_TO_SURFACE, "oppositeDirection" : true, "depth" : 25.4 * mm, "endBoundEntityFace" : qUnion([Q1]), "offsetDistance" : 25.4 * mm});
        }
        {
            var Q0;
            Q0 = qSketchRegion(id + "F29", true);
            var Q1;
            Q1=makeQuery(id+"F22.opExtrude","SWEPT_FACE",FACE,{"disambiguationData":[OSD([sQuery(id+"F15.wireOp",EDGE,"E34.right")])]});
            extrude(context, id + "F36", {"entities" : qUnion([Q0]), "endBound" : BoundingType.UP_TO_SURFACE, "oppositeDirection" : true, "depth" : 25.4 * mm, "endBoundEntityFace" : qUnion([Q1]), "offsetDistance" : 25.4 * mm});
        }
        {
            var Q0;
            Q0=makeQuery(id+"F22.opExtrude","CAP_EDGE",EDGE,{"disambiguationData":[OSD([sQuery(id+"F15.wireOp",EDGE,"E38")])],"isStart":false});
            var Q1;
            Q1=makeQuery(id+"F22.opExtrude","CAP_EDGE",EDGE,{"disambiguationData":[OSD([sQuery(id+"F15.wireOp",EDGE,"E38")])],"isStart":true});
            chamfer(context, id + "F37", {"entities" : qUnion([Q0, Q1]), "width" : 5.08 * mm, "tangentPropagation" : true});
        }
    });
